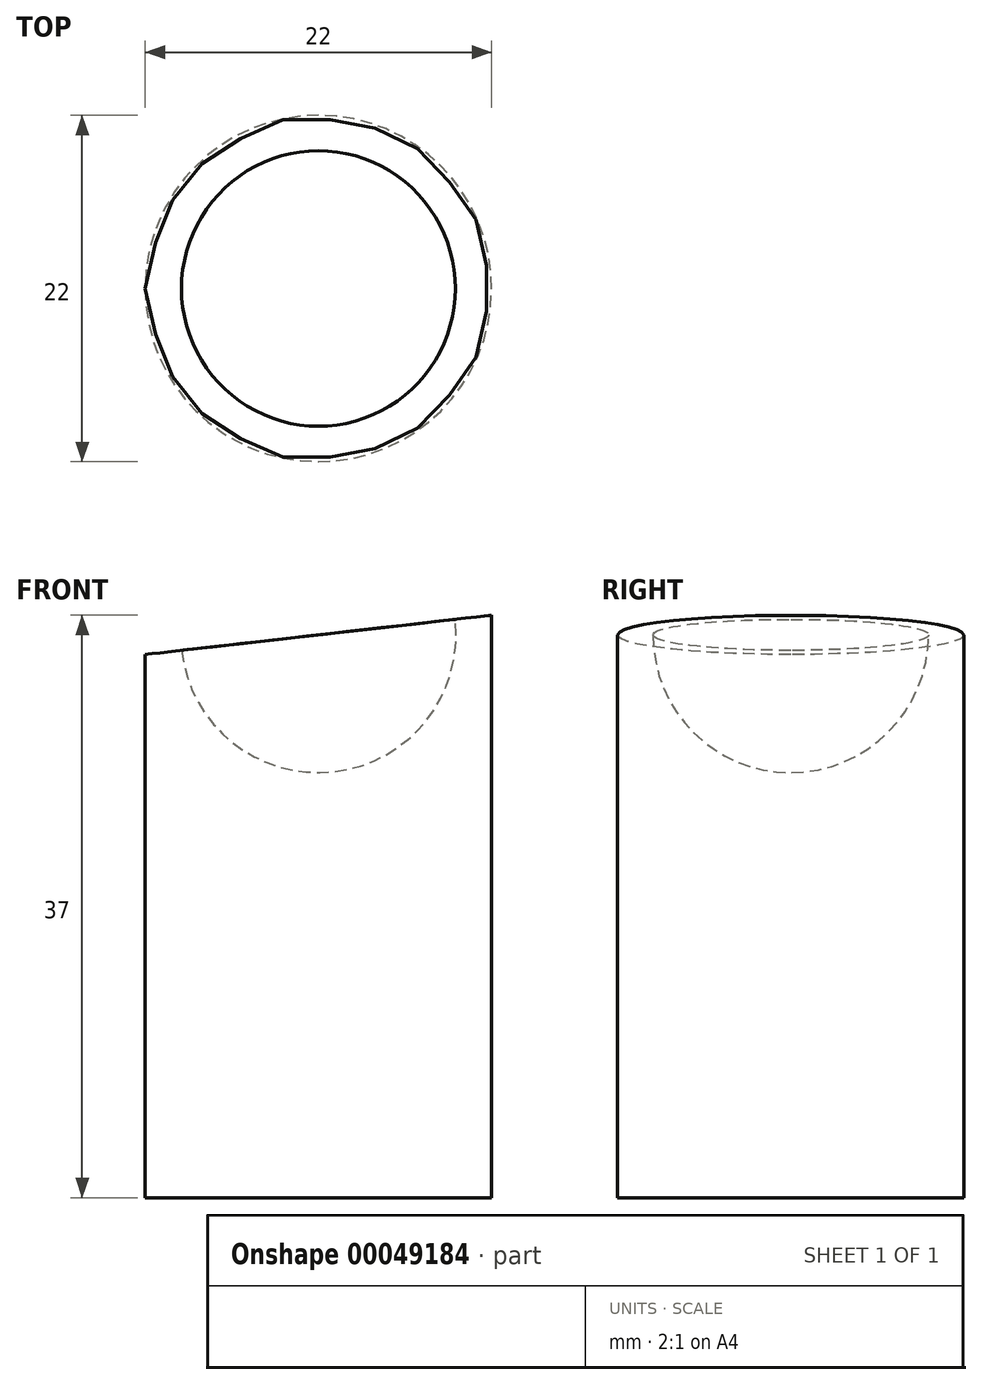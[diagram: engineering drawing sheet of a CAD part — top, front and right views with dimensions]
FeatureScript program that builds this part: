
annotation { "Feature Type Name" : "Feature", "Feature Type Description" : "" }
export const myFeature = defineFeature(function(context is Context, id is Id, definition is map)
    precondition{}
    {
        {
            var Q0;
            Q0=qCreatedBy(makeId("Top.planeOp"),FACE);
            var sketch = newSketch(context, id + "F0", { "sketchPlane" : qUnion([Q0])});
            skCircle(sketch, "E0", {"center": v(0, 0) * mm, "radius": 11 * mm});
            skSolve(sketch);
        }
        {
            var Q0;
            Q0 = qSketchRegion(id + "F0", true);
            extrude(context, id + "F1", {"entities" : qUnion([Q0]), "depth" : 37 * mm});
        }
        {
            var Q0;
            Q0=qCreatedBy(makeId("Front.planeOp"),FACE);
            var sketch = newSketch(context, id + "F2", { "sketchPlane" : qUnion([Q0])});
            skLineSegment(sketch, "E1.0", {"start": v(-11, 37) * mm, "end": v(11, 37) * mm});
            skLineSegment(sketch, "E2", {"start": v(11, 37) * mm, "end": v(-11, 34.5) * mm});
            skLineSegment(sketch, "E3", {"start": v(-11, 37) * mm, "end": v(-11, 34.5) * mm});
            skSolve(sketch);
        }
        {
            var Q0;
            Q0 = qSketchRegion(id + "F2", true);
            extrude(context, id + "F3", {"entities" : qUnion([Q0]), "operationType" : NewBodyOperationType.REMOVE, "endBound" : BoundingType.THROUGH_ALL, "oppositeDirection" : true, "depth" : 25 * mm, "hasSecondDirection" : true, "secondDirectionBound" : SecondDirectionBoundingType.THROUGH_ALL, "secondDirectionOppositeDirection" : false, "secondDirectionDepth" : 25 * mm});
        }
        {
            var Q0;
            Q0=makeQuery(id+"F3.boolean.opBoolean","COPY",FACE,{"derivedFrom":makeQuery(id+"F3.opExtrude","SWEPT_FACE",FACE,{"disambiguationData":[OSD([sQuery(id+"F2.wireOp",EDGE,"E2")])]})});
            var sketch = newSketch(context, id + "F4", { "sketchPlane" : qUnion([Q0])});
            skArc(sketch, "E4", {"start": v(-4.71, 0) * mm, "mid": v(4.04, -8.75) * mm, "end": v(12.79, 0) * mm});
            skLineSegment(sketch, "E5", {"start": v(-4.71, 0) * mm, "end": v(12.79, 0) * mm});
            skSolve(sketch);
        }
        {
            var Q0;
            Q0 = qSketchRegion(id + "F4", true);
            var Q1;
            Q1=sQuery(id+"F4.wireOp",EDGE,"E5");
            revolve(context, id + "F5", {"operationType" : NewBodyOperationType.REMOVE, "entities" : qUnion([Q0]), "axis" : qUnion([Q1]), "revolveType" : RevolveType.FULL, "oppositeDirection" : true});
        }
    });
